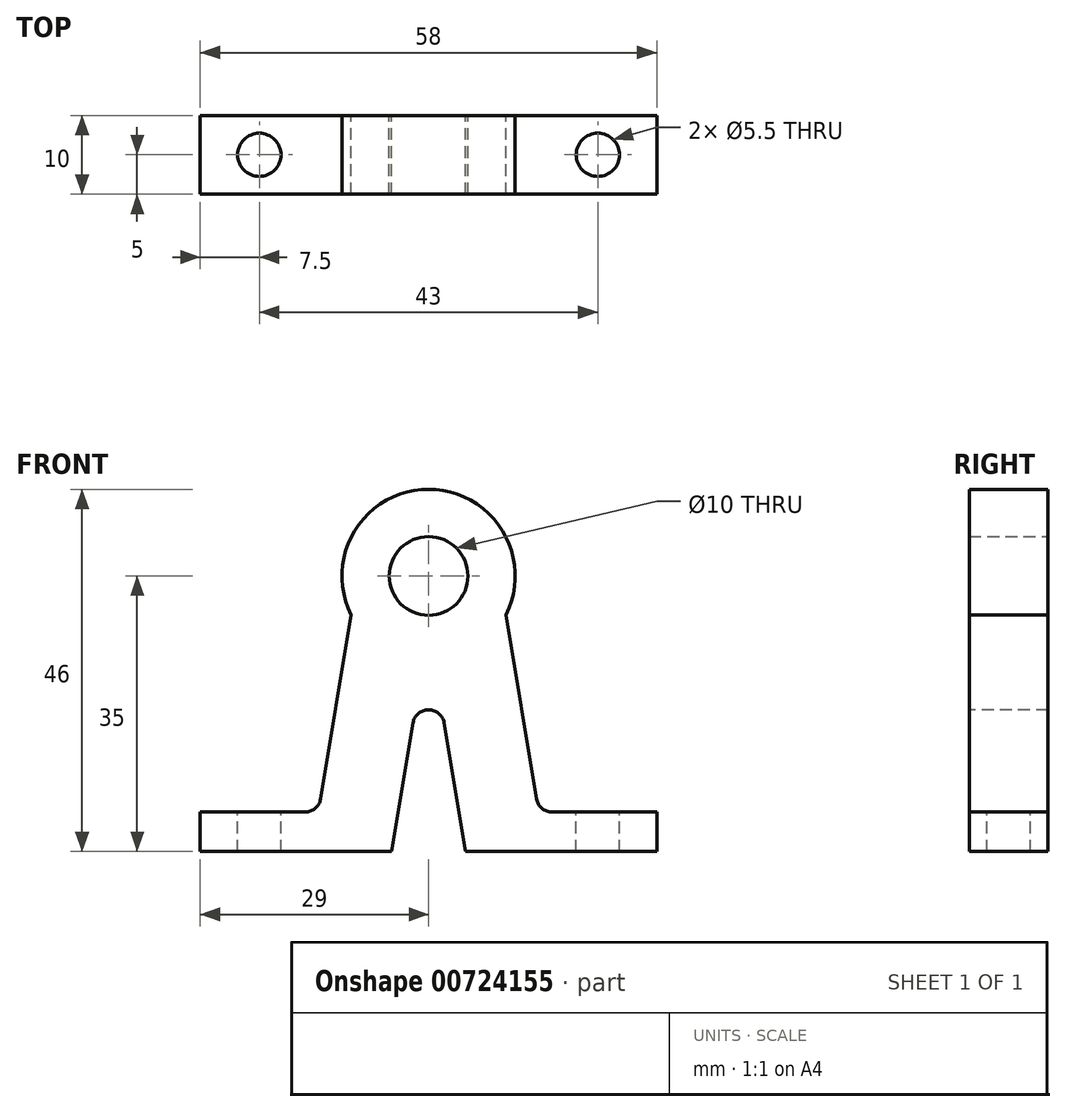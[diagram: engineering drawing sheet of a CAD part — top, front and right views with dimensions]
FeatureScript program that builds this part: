
annotation { "Feature Type Name" : "Feature", "Feature Type Description" : "" }
export const myFeature = defineFeature(function(context is Context, id is Id, definition is map)
    precondition{}
    {
        {
            var Q0;
            Q0=qCreatedBy(makeId("Front.planeOp"),FACE);
            var sketch = newSketch(context, id + "F0", { "sketchPlane" : qUnion([Q0])});
            skCircle(sketch, "E0", {"center": v(0, 0) * mm, "radius": 9 * mm});
            skCircle(sketch, "E1", {"center": v(0, 0) * mm, "radius": 5 * mm});
            skLineSegment(sketch, "E2", {"start": v(-29, -30) * mm, "end": v(-14, -30) * mm});
            skLineSegment(sketch, "E3", {"start": v(-14, -30) * mm, "end": v(-9, 0) * mm});
            skLineSegment(sketch, "E4", {"start": v(-29, -30) * mm, "end": v(-29, -35) * mm});
            skLineSegment(sketch, "E5", {"start": v(0, 0) * mm, "end": v(0, -14.3) * mm, "construction": true});
            skLineSegment(sketch, "E6.MirrorCS", {"start": v(14, -30) * mm, "end": v(9, 0) * mm});
            skLineSegment(sketch, "E7.MirrorCS", {"start": v(29, -30) * mm, "end": v(14, -30) * mm});
            skLineSegment(sketch, "E8.MirrorCS", {"start": v(29, -30) * mm, "end": v(29, -35) * mm});
            skLineSegment(sketch, "E9", {"start": v(-29, -35) * mm, "end": v(29, -35) * mm});
            skLineSegment(sketch, "E10", {"start": v(-4.7, -35) * mm, "end": v(0, -6.83) * mm});
            skLineSegment(sketch, "E11", {"start": v(0, -6.83) * mm, "end": v(4.7, -35) * mm});
            skSolve(sketch);
        }
        {
            var Q0;
            Q0=makeQuery(id+"F0.imprint","IMPRINT",FACE,{"disambiguationData":[TD([[makeQuery(id+"F0.imprint","IMPRINT",EDGE,{"derivedFrom":sQuery(id+"F0.wireOp",EDGE,"E2")}),-1.0]])]});
            var Q1;
            Q1=makeQuery(id+"F0.imprint","IMPRINT",FACE,{"disambiguationData":[TD([[makeQuery(id+"F0.imprint","IMPRINT",EDGE,{"derivedFrom":sQuery(id+"F0.wireOp",EDGE,"E1")}),-1.0]])]});
            var Q2;
            {var subQ1=sQuery(id+"F0.wireOp",EDGE,"E6.MirrorCS");Q2=makeQuery(id+"F0.imprint","IMPRINT",FACE,{"disambiguationData":[TD([[makeQuery(id+"F0.imprint","IMPRINT",EDGE,{"derivedFrom":subQ1}),1.0]])]});}
            extrude(context, id + "F1", {"entities" : qUnion([Q0, Q1, Q2]), "depth" : 10 * mm, "offsetDistance" : 25 * mm});
        }
        {
            var Q0;
            Q0=makeQuery(id+"F1.opExtrude","SWEPT_FACE",FACE,{"disambiguationData":[OSD([sQuery(id+"F0.wireOp",EDGE,"E2")])]});
            var sketch = newSketch(context, id + "F2", { "sketchPlane" : qUnion([Q0])});
            skLineSegment(sketch, "E12", {"start": v(-29, 0) * mm, "end": v(-14, -10) * mm, "construction": true});
            skLineSegment(sketch, "E13", {"start": v(29, 0) * mm, "end": v(14, -10) * mm, "construction": true});
            skCircle(sketch, "E14", {"center": v(-21.5, -5) * mm, "radius": 2.75 * mm});
            skCircle(sketch, "E15", {"center": v(21.5, -5) * mm, "radius": 2.75 * mm});
            skSolve(sketch);
        }
        {
            var Q0;
            Q0=makeQuery(id+"F2.imprint","IMPRINT",FACE,{"disambiguationData":[TD([[makeQuery(id+"F2.imprint","IMPRINT",EDGE,{"derivedFrom":sQuery(id+"F2.wireOp",EDGE,"E14")}),1.0]])]});
            var Q1;
            Q1=makeQuery(id+"F2.imprint","IMPRINT",FACE,{"disambiguationData":[TD([[makeQuery(id+"F2.imprint","IMPRINT",EDGE,{"derivedFrom":sQuery(id+"F2.wireOp",EDGE,"E15")}),1.0]])]});
            extrude(context, id + "F3", {"entities" : qUnion([Q0, Q1]), "operationType" : NewBodyOperationType.REMOVE, "endBound" : BoundingType.THROUGH_ALL, "oppositeDirection" : true, "depth" : 25 * mm, "offsetDistance" : 25 * mm});
        }
        {
            var Q0;
            Q0=makeQuery(id+"F1.opExtrude","CAP_FACE",FACE,{"disambiguationData":[OSD([sQuery(id+"F0.wireOp",EDGE,"E0"),sQuery(id+"F0.wireOp",EDGE,"E1"),sQuery(id+"F0.wireOp",EDGE,"E2"),sQuery(id+"F0.wireOp",EDGE,"E3"),sQuery(id+"F0.wireOp",EDGE,"E4"),sQuery(id+"F0.wireOp",EDGE,"E6.MirrorCS"),sQuery(id+"F0.wireOp",EDGE,"E7.MirrorCS"),sQuery(id+"F0.wireOp",EDGE,"E8.MirrorCS"),sQuery(id+"F0.wireOp",EDGE,"E9"),sQuery(id+"F0.wireOp",EDGE,"E10"),sQuery(id+"F0.wireOp",EDGE,"E11")])],"isStart":true});
            var sketch = newSketch(context, id + "F4", { "sketchPlane" : qUnion([Q0])});
            skCircle(sketch, "E16", {"center": v(0, 0) * mm, "radius": 11 * mm});
            skCircle(sketch, "E17", {"center": v(0, 0) * mm, "radius": 5 * mm});
            skSolve(sketch);
        }
        {
            var Q0;
            {var subQ5=makeQuery(id+"F1.opExtrude","CAP_EDGE",EDGE,{"disambiguationData":[OSD([sQuery(id+"F0.wireOp",EDGE,"E0")])],"isStart":true});Q0=makeQuery(id+"F4.imprint","IMPRINT",FACE,{"disambiguationData":[TD([[makeQuery(id+"F4.imprint","IMPRINT",EDGE,{"derivedFrom":subQ5}),1.0]])]});}
            var Q1;
            Q1=makeQuery(id+"F1.opExtrude","CAP_FACE",FACE,{"disambiguationData":[OSD([sQuery(id+"F0.wireOp",EDGE,"E0"),sQuery(id+"F0.wireOp",EDGE,"E1"),sQuery(id+"F0.wireOp",EDGE,"E2"),sQuery(id+"F0.wireOp",EDGE,"E3"),sQuery(id+"F0.wireOp",EDGE,"E4"),sQuery(id+"F0.wireOp",EDGE,"E6.MirrorCS"),sQuery(id+"F0.wireOp",EDGE,"E7.MirrorCS"),sQuery(id+"F0.wireOp",EDGE,"E8.MirrorCS"),sQuery(id+"F0.wireOp",EDGE,"E9"),sQuery(id+"F0.wireOp",EDGE,"E10"),sQuery(id+"F0.wireOp",EDGE,"E11")])],"isStart":false});
            extrude(context, id + "F5", {"entities" : qUnion([Q0]), "operationType" : NewBodyOperationType.ADD, "endBound" : BoundingType.UP_TO_SURFACE, "oppositeDirection" : true, "depth" : 25 * mm, "endBoundEntityFace" : qUnion([Q1]), "offsetDistance" : 25 * mm});
        }
        {
            var Q0;
            Q0=makeQuery(id+"F1.opExtrude","SWEPT_EDGE",EDGE,{"disambiguationData":[OSD([sQuery(id+"F0.wireOp",EDGE,"E10"),sQuery(id+"F0.wireOp",EDGE,"E11")])]});
            var Q1;
            Q1=makeQuery(id+"F1.opExtrude","SWEPT_EDGE",EDGE,{"disambiguationData":[OSD([sQuery(id+"F0.wireOp",EDGE,"E2"),sQuery(id+"F0.wireOp",EDGE,"E3")])]});
            var Q2;
            Q2=makeQuery(id+"F1.opExtrude","SWEPT_EDGE",EDGE,{"disambiguationData":[OSD([sQuery(id+"F0.wireOp",EDGE,"E6.MirrorCS"),sQuery(id+"F0.wireOp",EDGE,"E7.MirrorCS")])]});
            var Q3;
            Q3=makeQuery(id+"F5.opExtrude","SWEPT_EDGE",EDGE,{"disambiguationData":[OSD([sQuery(id+"F0.wireOp",EDGE,"E6.MirrorCS"),sQuery(id+"F4.wireOp",EDGE,"E16")])]});
            var Q4;
            Q4=makeQuery(id+"F5.opExtrude","SWEPT_EDGE",EDGE,{"disambiguationData":[OSD([sQuery(id+"F0.wireOp",EDGE,"E3"),sQuery(id+"F4.wireOp",EDGE,"E16")])]});
            fillet(context, id + "F6", {"entities" : qUnion([Q0, Q1, Q2, Q3, Q4]), "radius" : 2 * mm, "tangentPropagation" : true, "allowEdgeOverflow" : false});
        }
    });
